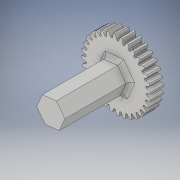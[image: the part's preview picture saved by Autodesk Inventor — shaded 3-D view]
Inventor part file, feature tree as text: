
AUTODESK INVENTOR PART (.ipt)
format: ipt  version: 2019 (Build 230136000, 136)  size: 763,904 bytes
history: native  units: in
note: dims shown in document units (in); Inventor stores cm internally (conversion verified against a paired STEP export)
features: extrude x3, projected_geometry x2, sketch x2, fillet x1, other x1
ambient origin geometry x8: Origin, YZ Plane, XZ Plane, XY Plane, X Axis, Y Axis, Z Axis, Center Point
bodies: Solid1 (feature_tree)
feature tree (9):
  extrude  "Extrusion1"  Depth=0.25in
  extrude  "Extrusion2"  Depth=0.375in
  extrude  "Extrusion3"  Depth=1.0in TaperAngle=0.0deg
  fillet  "Fillet1"  Radius=0.2in
  projected_geometry  "Projected Loop1"
  sketch  "Sketch2"  dims[d0=0.01in d1=0.0in d2=0.25in]
  sketch  "Sketch3"  dims[d3=0.2in d4=0.0in d5=0.375in d6=1.0in d7=0.0in d8=0.2in d9=0.0in d10=0.0625in]
  projected_geometry  "Projected Loop2"
  other  "bore"
